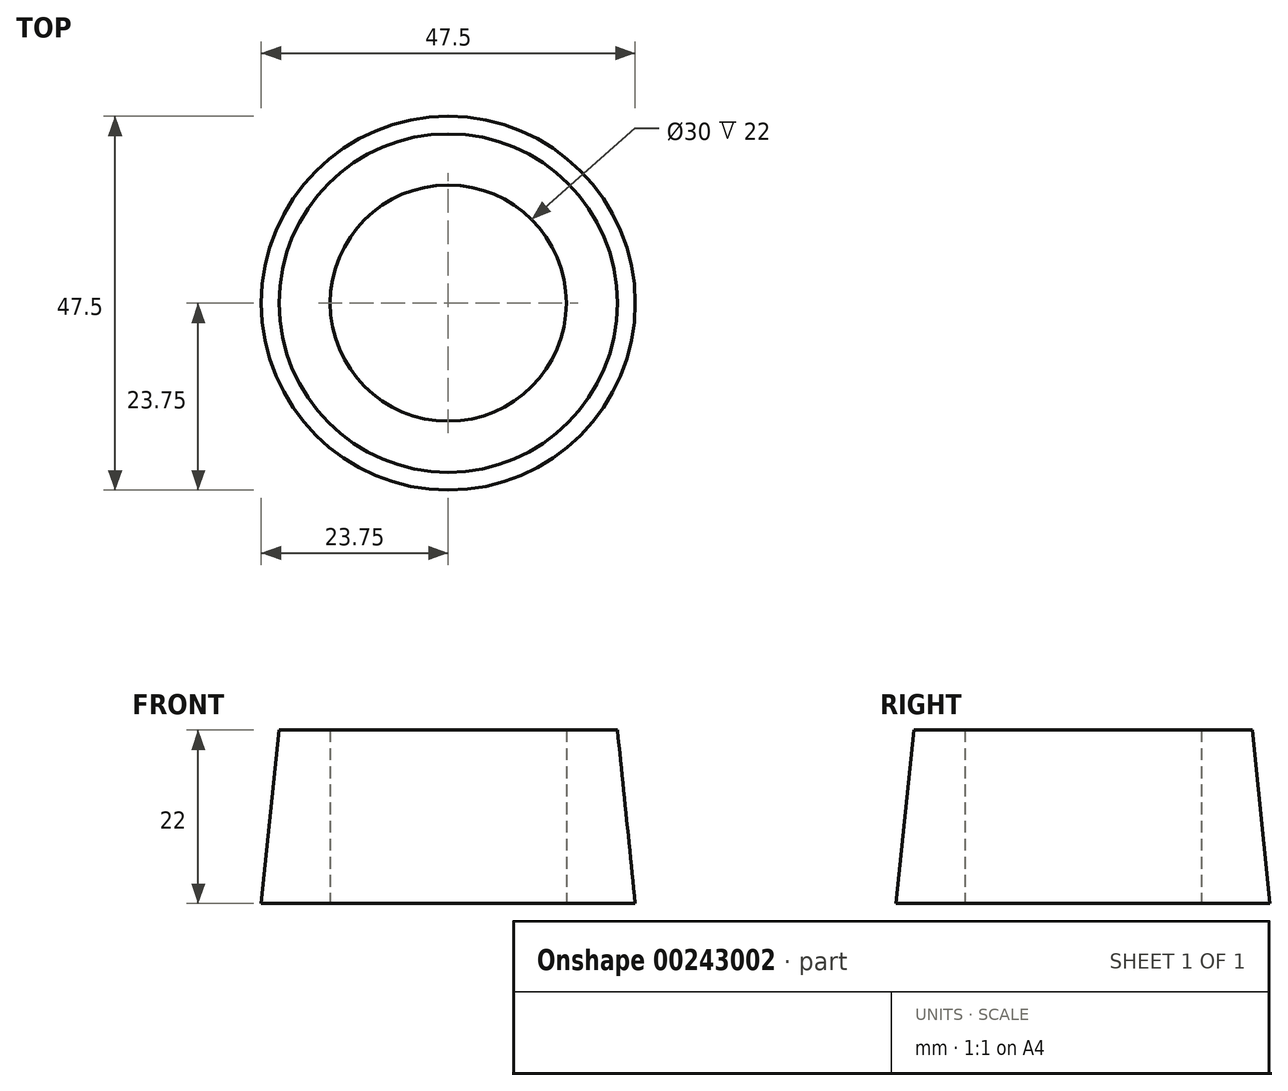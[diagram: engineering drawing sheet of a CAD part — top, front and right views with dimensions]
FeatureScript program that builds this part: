
annotation { "Feature Type Name" : "Feature", "Feature Type Description" : "" }
export const myFeature = defineFeature(function(context is Context, id is Id, definition is map)
    precondition{}
    {
        {
            var Q0;
            Q0=qCreatedBy(makeId("Top.planeOp"),FACE);
            var sketch = newSketch(context, id + "F0", { "sketchPlane" : qUnion([Q0])});
            skCircle(sketch, "E0", {"center": v(0, 0) * mm, "radius": 15 * mm});
            skCircle(sketch, "E1", {"center": v(0, 0) * mm, "radius": 23.75 * mm});
            skSolve(sketch);
        }
        {
            var Q0;
            Q0 = qSketchRegion(id + "F0", true);
            extrude(context, id + "F1", {"entities" : qUnion([Q0]), "depth" : 22 * mm});
        }
        {
            var Q0;
            Q0=qCreatedBy(makeId("Front.planeOp"),FACE);
            var sketch = newSketch(context, id + "F2", { "sketchPlane" : qUnion([Q0])});
            skLineSegment(sketch, "E2", {"start": v(-23.75, 0) * mm, "end": v(-23.75, 28.32) * mm});
            skLineSegment(sketch, "E3", {"start": v(-23.75, 28.32) * mm, "end": v(-20.85, 28.32) * mm});
            skLineSegment(sketch, "E4", {"start": v(-20.85, 28.32) * mm, "end": v(-23.75, 0) * mm});
            skLineSegment(sketch, "E5", {"start": v(0, 0) * mm, "end": v(0, 34.93) * mm});
            skSolve(sketch);
        }
        {
            var Q0;
            Q0 = qSketchRegion(id + "F2", true);
            var Q1;
            Q1=sQuery(id+"F2.wireOp",EDGE,"E5");
            revolve(context, id + "F3", {"operationType" : NewBodyOperationType.REMOVE, "entities" : qUnion([Q0]), "axis" : qUnion([Q1]), "revolveType" : RevolveType.FULL, "oppositeDirection" : true});
        }
    });
